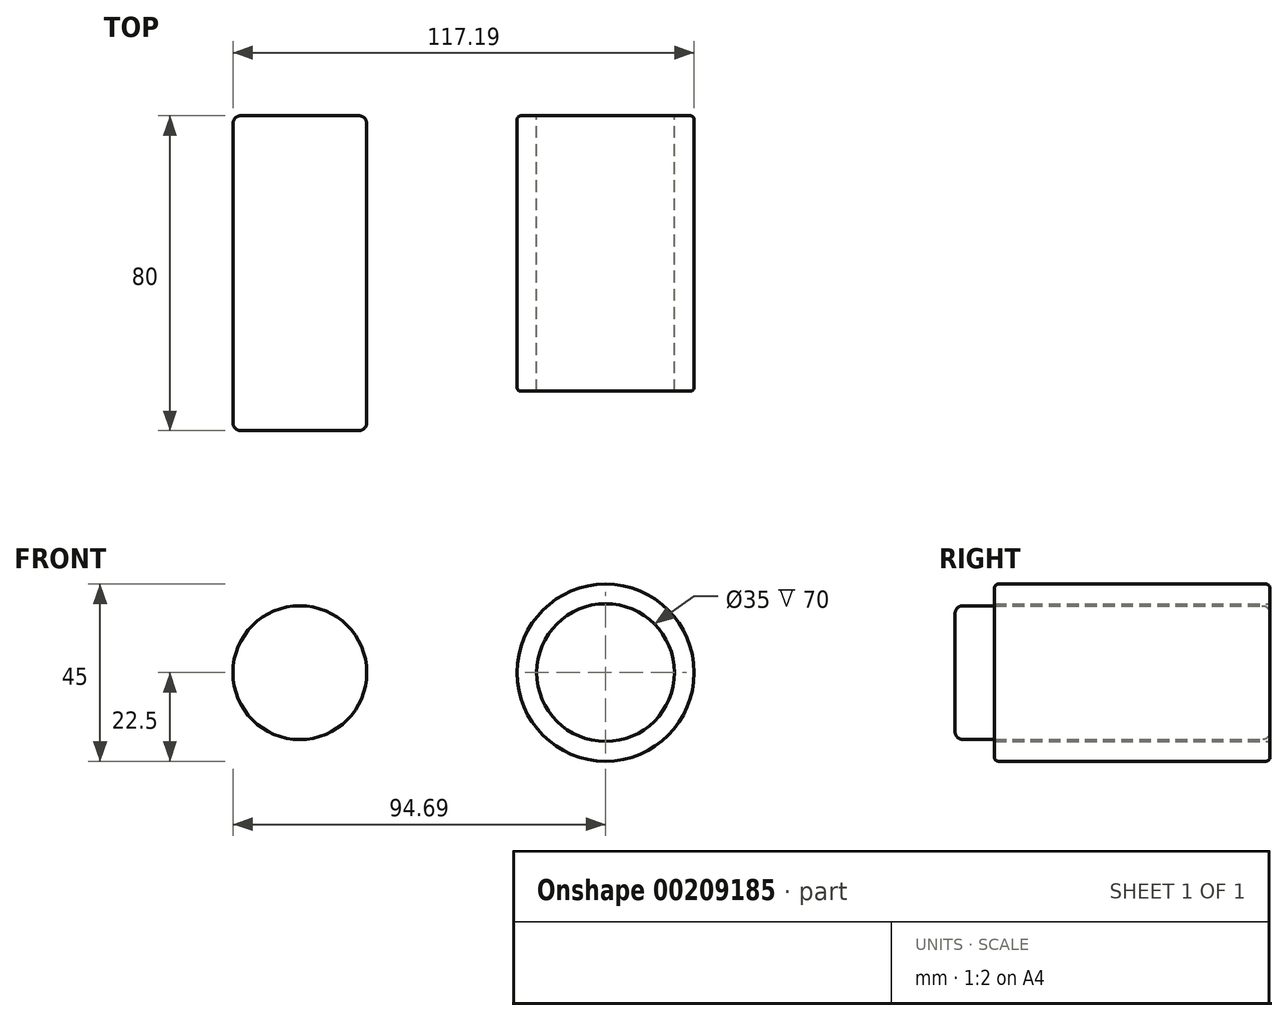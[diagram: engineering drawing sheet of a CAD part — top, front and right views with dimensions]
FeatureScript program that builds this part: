
annotation { "Feature Type Name" : "Feature", "Feature Type Description" : "" }
export const myFeature = defineFeature(function(context is Context, id is Id, definition is map)
    precondition{}
    {
        {
            var Q0;
            Q0=qCreatedBy(makeId("Front.planeOp"),FACE);
            var sketch = newSketch(context, id + "F0", { "sketchPlane" : qUnion([Q0])});
            skCircle(sketch, "E0", {"center": v(0, 0) * mm, "radius": 17.5 * mm});
            skArc(sketch, "E1", {"start": v(-22.48, 0.9) * mm, "mid": v(-18.94, -12.15) * mm, "end": v(-8.56, -20.8) * mm});
            skArc(sketch, "E2", {"start": v(-8.56, -20.8) * mm, "mid": v(18.94, 12.15) * mm, "end": v(-22.48, 0.9) * mm});
            skSolve(sketch);
        }
        {
            var Q0;
            Q0 = qSketchRegion(id + "F0", true);
            extrude(context, id + "F1", {"entities" : qUnion([Q0]), "depth" : 70 * mm});
        }
        {
            var Q0;
            Q0=makeQuery(id+"F1.opExtrude","CAP_EDGE",EDGE,{"disambiguationData":[OSD([sQuery(id+"F0.wireOp",EDGE,"E1"),sQuery(id+"F0.wireOp",EDGE,"E2")])],"isStart":true});
            var Q1;
            Q1=makeQuery(id+"F1.opExtrude","CAP_EDGE",EDGE,{"disambiguationData":[OSD([sQuery(id+"F0.wireOp",EDGE,"E1"),sQuery(id+"F0.wireOp",EDGE,"E2")])],"isStart":false});
            fillet(context, id + "F2", {"entities" : qUnion([Q0, Q1]), "radius" : 1 * mm, "tangentPropagation" : true, "allowEdgeOverflow" : false});
        }
        {
            var Q0;
            Q0=qCreatedBy(makeId("Front.planeOp"),FACE);
            var sketch = newSketch(context, id + "F3", { "sketchPlane" : qUnion([Q0])});
            skCircle(sketch, "E3", {"center": v(-77.69, 0) * mm, "radius": 17 * mm});
            skSolve(sketch);
        }
        {
            var Q0;
            Q0 = qSketchRegion(id + "F3", true);
            extrude(context, id + "F4", {"entities" : qUnion([Q0]), "depth" : 80 * mm});
        }
        {
            var Q0;
            Q0=makeQuery(id+"F4.opExtrude","CAP_EDGE",EDGE,{"disambiguationData":[OSD([sQuery(id+"F3.wireOp",EDGE,"E3")])],"isStart":false});
            var Q1;
            Q1=makeQuery(id+"F4.opExtrude","CAP_EDGE",EDGE,{"disambiguationData":[OSD([sQuery(id+"F3.wireOp",EDGE,"E3")])],"isStart":true});
            fillet(context, id + "F5", {"entities" : qUnion([Q0, Q1]), "radius" : 2 * mm, "tangentPropagation" : true, "allowEdgeOverflow" : false});
        }
    });
